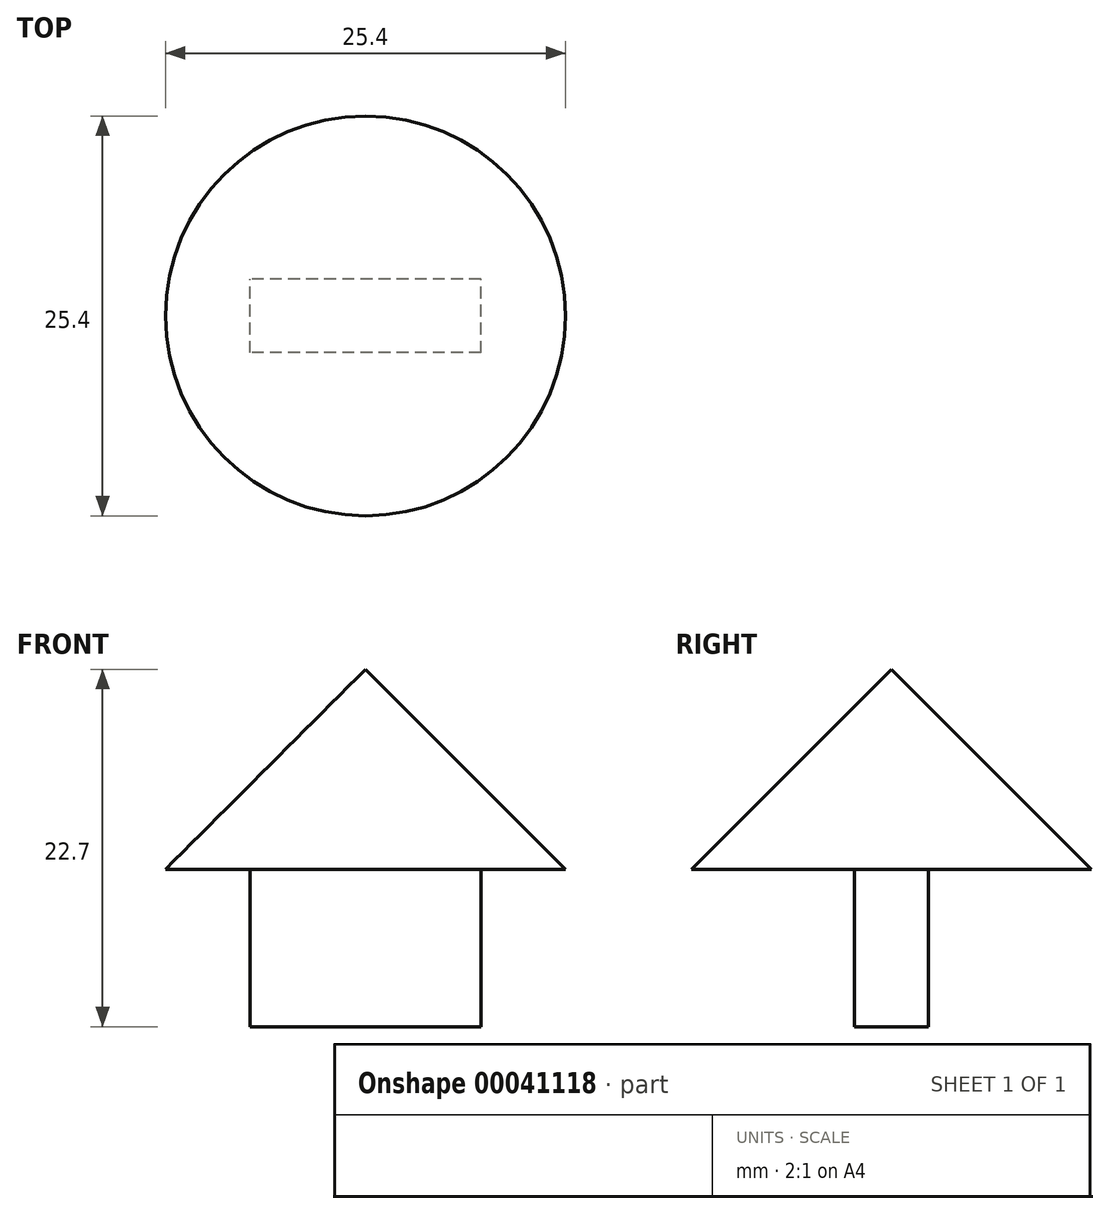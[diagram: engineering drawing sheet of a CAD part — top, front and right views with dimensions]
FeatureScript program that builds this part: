
annotation { "Feature Type Name" : "Feature", "Feature Type Description" : "" }
export const myFeature = defineFeature(function(context is Context, id is Id, definition is map)
    precondition{}
    {
        {
            var Q0;
            Q0=qCreatedBy(makeId("Front.planeOp"),FACE);
            var sketch = newSketch(context, id + "F0", { "sketchPlane" : qUnion([Q0])});
            skLineSegment(sketch, "E0", {"start": v(0, 0) * mm, "end": v(0, 12.7) * mm});
            skLineSegment(sketch, "E1", {"start": v(0, 12.7) * mm, "end": v(12.7, 0) * mm});
            skLineSegment(sketch, "E2", {"start": v(0, 0) * mm, "end": v(12.7, 0) * mm});
            skSolve(sketch);
        }
        {
            var Q0;
            Q0=qCreatedBy(makeId("Front.planeOp"),FACE);
            var sketch = newSketch(context, id + "F1", { "sketchPlane" : qUnion([Q0])});
            skLineSegment(sketch, "E3", {"start": v(0, 0) * mm, "end": v(0, 39.86) * mm});
            skSolve(sketch);
        }
        {
            var Q0;
            Q0 = qSketchRegion(id + "F0", true);
            var Q1;
            Q1=sQuery(id+"F1.wireOp",EDGE,"E3");
            revolve(context, id + "F2", {"entities" : qUnion([Q0]), "axis" : qUnion([Q1]), "revolveType" : RevolveType.FULL});
        }
        {
            var Q0;
            Q0=qCreatedBy(makeId("Top.planeOp"),FACE);
            var sketch = newSketch(context, id + "F3", { "sketchPlane" : qUnion([Q0])});
            skLineSegment(sketch, "E4.rect.bottom", {"start": v(7.33, -2.34) * mm, "end": v(-7.33, -2.34) * mm});
            skLineSegment(sketch, "E4.rect.top", {"start": v(7.33, 2.34) * mm, "end": v(-7.33, 2.34) * mm});
            skLineSegment(sketch, "E4.rect.left", {"start": v(7.33, -2.34) * mm, "end": v(7.33, 2.34) * mm});
            skLineSegment(sketch, "E4.rect.right", {"start": v(-7.33, -2.34) * mm, "end": v(-7.33, 2.34) * mm});
            skPoint(sketch, "E4.rect.middle", {"position": v(0, 0) * mm});
            skSolve(sketch);
        }
        {
            var Q0;
            Q0=makeQuery(id+"F3.imprint","IMPRINT",FACE,{"disambiguationData":[TD([[makeQuery(id+"F3.imprint","IMPRINT",EDGE,{"derivedFrom":sQuery(id+"F3.wireOp",EDGE,"E4.rect.bottom")}),-1.0]])]});
            extrude(context, id + "F4", {"entities" : qUnion([Q0]), "operationType" : NewBodyOperationType.ADD, "oppositeDirection" : true, "depth" : 10 * mm});
        }
    });
